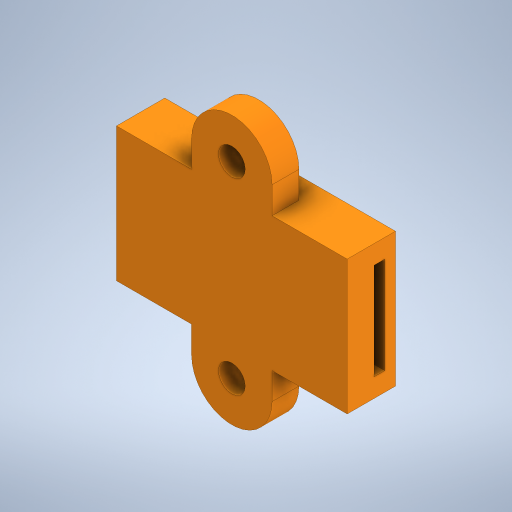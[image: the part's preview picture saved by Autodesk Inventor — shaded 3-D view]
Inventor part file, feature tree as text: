
AUTODESK INVENTOR PART (.ipt)
format: ipt  version: 2023 (Build 270158000, 158)  size: 287,744 bytes
history: native  units: mm
features: extrude x3, sketch x3
ambient origin geometry x8: Origin, YZ Plane, XZ Plane, XY Plane, X Axis, Y Axis, Z Axis, Center Point
bodies: Solid1 (feature_tree)
feature tree (6):
  extrude  "Extrusion1"  Depth=25.0mm
  extrude  "Extrusion2"  Depth=15.0mm
  extrude  "Extrusion3"  Depth=21.5mm
  sketch  "Sketch1"  dims[d0=43.0mm d1=25.0mm]
  sketch  "Sketch2"  dims[d2=15.0mm d3=15.0mm]
  sketch  "Sketch3"  dims[d4=21.5mm d5=21.5mm d6=5.0mm d7=5.0mm d8=5.0mm d9=5.0mm d10=5.0mm d11=0.0mm d12=3.5mm d13=3.5mm d14=2.0mm d15=0.0mm d16=4.0mm d17=4.0mm d18=0.0mm d19=2.0mm d20=2.0mm d21=2.0mm d22=0.0mm]
